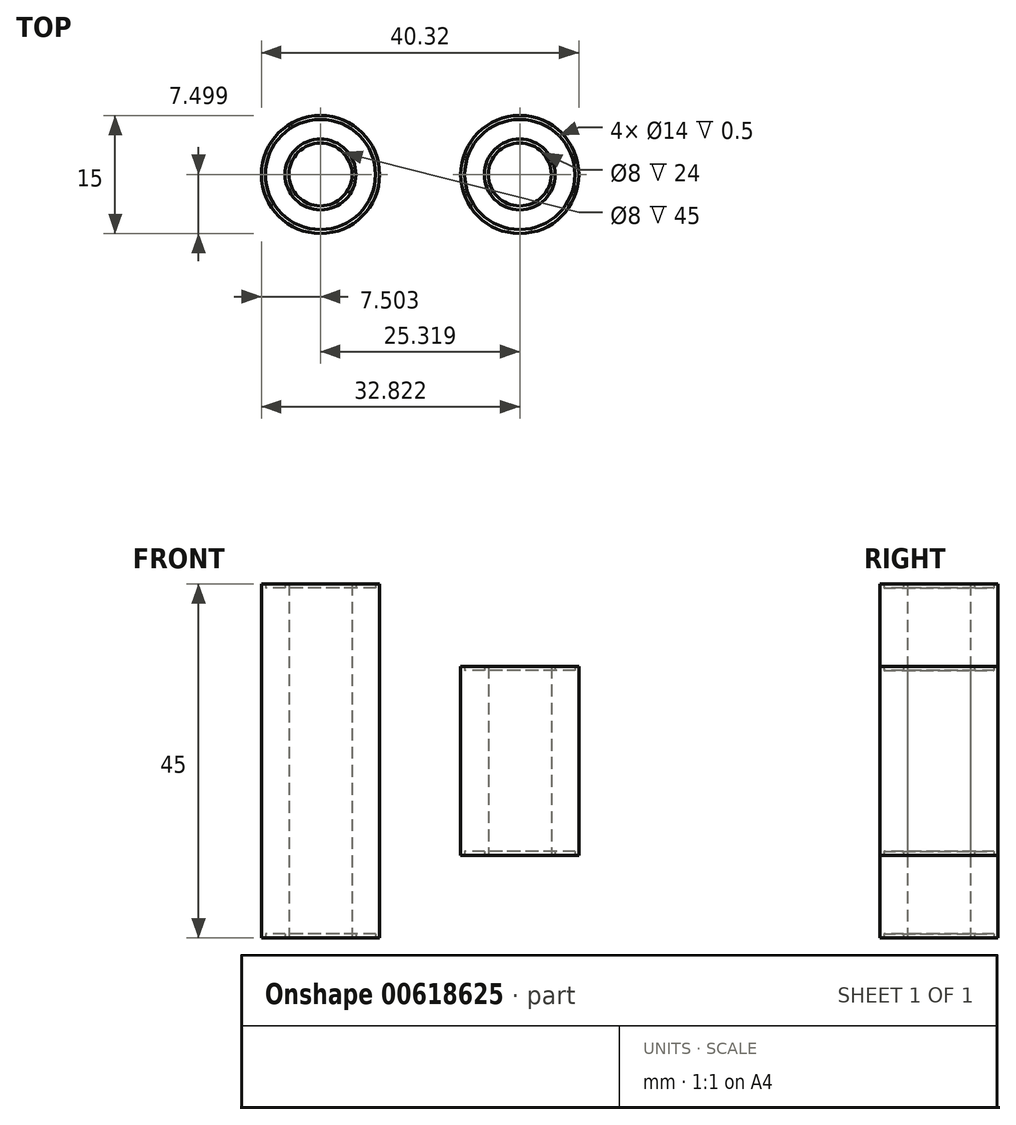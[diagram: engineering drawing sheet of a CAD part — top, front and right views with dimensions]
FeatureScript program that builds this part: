
annotation { "Feature Type Name" : "Feature", "Feature Type Description" : "" }
export const myFeature = defineFeature(function(context is Context, id is Id, definition is map)
    precondition{}
    {
        {
            var Q0;
            Q0=qCreatedBy(makeId("Top.planeOp"),FACE);
            var sketch = newSketch(context, id + "F0", { "sketchPlane" : qUnion([Q0])});
            skCircle(sketch, "E0", {"center": v(-34.69, -24.85) * mm, "radius": 7.5 * mm});
            skCircle(sketch, "E1", {"center": v(-34.69, -24.85) * mm, "radius": 4 * mm});
            skCircle(sketch, "E2", {"center": v(-34.69, -24.85) * mm, "radius": 7 * mm});
            skCircle(sketch, "E3", {"center": v(-34.69, -24.85) * mm, "radius": 4.5 * mm});
            skCircle(sketch, "E4", {"center": v(-9.37, -24.85) * mm, "radius": 7.5 * mm});
            skCircle(sketch, "E5", {"center": v(-9.37, -24.85) * mm, "radius": 4 * mm});
            skCircle(sketch, "E6", {"center": v(-9.37, -24.85) * mm, "radius": 7 * mm});
            skCircle(sketch, "E7", {"center": v(-9.37, -24.85) * mm, "radius": 4.5 * mm});
            skSolve(sketch);
        }
        {
            var Q0;
            Q0=makeQuery(id+"F0.imprint","IMPRINT",FACE,{"disambiguationData":[TD([[makeQuery(id+"F0.imprint","IMPRINT",EDGE,{"derivedFrom":sQuery(id+"F0.wireOp",EDGE,"E2")}),1.0]])]});
            extrude(context, id + "F1", {"entities" : qUnion([Q0]), "endBound" : BoundingType.SYMMETRIC, "depth" : 44 * mm, "offsetDistance" : 25 * mm});
        }
        {
            var Q0;
            Q0=makeQuery(id+"F0.imprint","IMPRINT",FACE,{"disambiguationData":[TD([[makeQuery(id+"F0.imprint","IMPRINT",EDGE,{"derivedFrom":sQuery(id+"F0.wireOp",EDGE,"E1")}),-1.0]])]});
            var Q1;
            Q1=makeQuery(id+"F0.imprint","IMPRINT",FACE,{"disambiguationData":[TD([[makeQuery(id+"F0.imprint","IMPRINT",EDGE,{"derivedFrom":sQuery(id+"F0.wireOp",EDGE,"E0")}),1.0]])]});
            extrude(context, id + "F2", {"entities" : qUnion([Q0, Q1]), "operationType" : NewBodyOperationType.ADD, "endBound" : BoundingType.SYMMETRIC, "depth" : 45 * mm, "offsetDistance" : 25 * mm});
        }
        {
            var Q0;
            Q0=makeQuery(id+"F0.imprint","IMPRINT",FACE,{"disambiguationData":[TD([[makeQuery(id+"F0.imprint","IMPRINT",EDGE,{"derivedFrom":sQuery(id+"F0.wireOp",EDGE,"E6")}),1.0]])]});
            extrude(context, id + "F3", {"entities" : qUnion([Q0]), "endBound" : BoundingType.SYMMETRIC, "depth" : 23 * mm, "offsetDistance" : 25 * mm});
        }
        {
            var Q0;
            Q0=makeQuery(id+"F0.imprint","IMPRINT",FACE,{"disambiguationData":[TD([[makeQuery(id+"F0.imprint","IMPRINT",EDGE,{"derivedFrom":sQuery(id+"F0.wireOp",EDGE,"E5")}),-1.0]])]});
            var Q1;
            Q1=makeQuery(id+"F0.imprint","IMPRINT",FACE,{"disambiguationData":[TD([[makeQuery(id+"F0.imprint","IMPRINT",EDGE,{"derivedFrom":sQuery(id+"F0.wireOp",EDGE,"E4")}),1.0]])]});
            extrude(context, id + "F4", {"entities" : qUnion([Q0, Q1]), "operationType" : NewBodyOperationType.ADD, "endBound" : BoundingType.SYMMETRIC, "depth" : 24 * mm, "offsetDistance" : 25 * mm});
        }
    });
